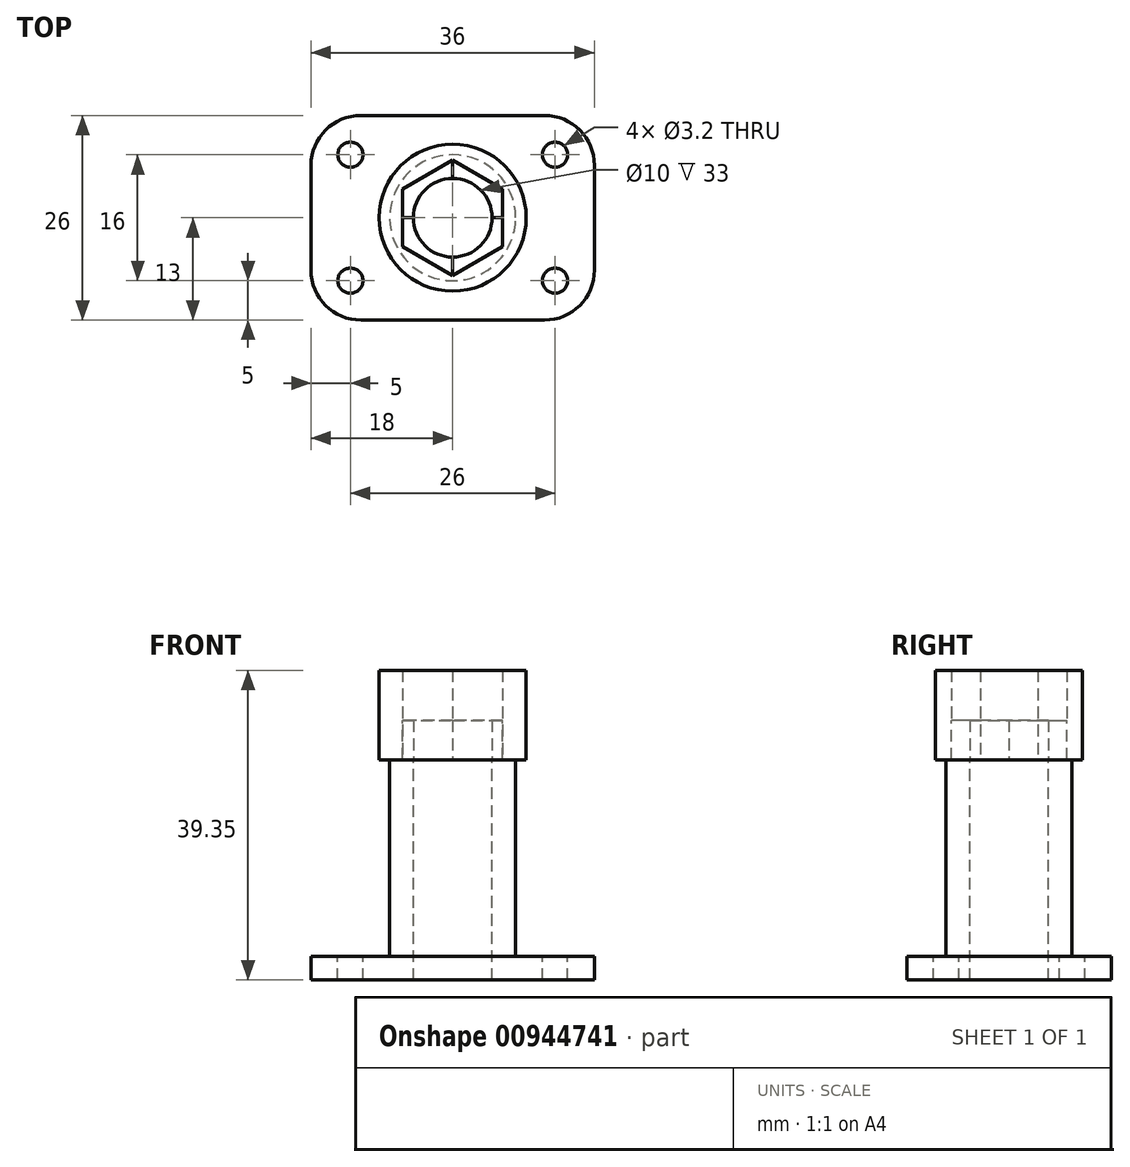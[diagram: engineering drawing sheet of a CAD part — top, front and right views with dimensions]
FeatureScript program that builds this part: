
annotation { "Feature Type Name" : "Feature", "Feature Type Description" : "" }
export const myFeature = defineFeature(function(context is Context, id is Id, definition is map)
    precondition{}
    {
        {
            var Q0;
            Q0=qCreatedBy(makeId("Top.planeOp"),FACE);
            var sketch = newSketch(context, id + "F0", { "sketchPlane" : qUnion([Q0])});
            skPoint(sketch, "E0.middle", {"position": v(0, 0) * mm});
            skCircle(sketch, "E1", {"center": v(0, 0) * mm, "radius": 5 * mm});
            skCircle(sketch, "E2.0", {"center": v(0, 0) * mm, "radius": 8 * mm});
            skLineSegment(sketch, "E3.bottom", {"start": v(-13, -8) * mm, "end": v(13, -8) * mm, "construction": true});
            skLineSegment(sketch, "E3.top", {"start": v(-13, 8) * mm, "end": v(13, 8) * mm, "construction": true});
            skLineSegment(sketch, "E3.left", {"start": v(-13, -8) * mm, "end": v(-13, 8) * mm, "construction": true});
            skLineSegment(sketch, "E3.right", {"start": v(13, -8) * mm, "end": v(13, 8) * mm, "construction": true});
            skLineSegment(sketch, "E4.0", {"start": v(-18, -6.65) * mm, "end": v(-18, 6.65) * mm});
            skLineSegment(sketch, "E4.1", {"start": v(-11.65, -13) * mm, "end": v(11.65, -13) * mm});
            skLineSegment(sketch, "E4.2", {"start": v(18, -6.65) * mm, "end": v(18, 6.65) * mm});
            skLineSegment(sketch, "E4.3", {"start": v(-11.65, 13) * mm, "end": v(11.65, 13) * mm});
            skPoint(sketch, "E5.visualSharp", {"position": v(-18, 13) * mm});
            skArc(sketch, "E5.filletArc", {"start": v(-11.65, 13) * mm, "mid": v(-16.14, 11.14) * mm, "end": v(-18, 6.65) * mm});
            skPoint(sketch, "E6.visualSharp", {"position": v(18, 13) * mm});
            skArc(sketch, "E6.filletArc", {"start": v(18, 6.65) * mm, "mid": v(16.14, 11.14) * mm, "end": v(11.65, 13) * mm});
            skPoint(sketch, "E7.visualSharp", {"position": v(18, -13) * mm});
            skArc(sketch, "E7.filletArc", {"start": v(11.65, -13) * mm, "mid": v(16.14, -11.14) * mm, "end": v(18, -6.65) * mm});
            skPoint(sketch, "E8.visualSharp", {"position": v(-18, -13) * mm});
            skArc(sketch, "E8.filletArc", {"start": v(-18, -6.65) * mm, "mid": v(-16.14, -11.14) * mm, "end": v(-11.65, -13) * mm});
            skLineSegment(sketch, "E9", {"start": v(0, 0) * mm, "end": v(-5, 0) * mm, "construction": true});
            skLineSegment(sketch, "E10", {"start": v(0, 0) * mm, "end": v(5, 0) * mm, "construction": true});
            skLineSegment(sketch, "E11", {"start": v(0, 0) * mm, "end": v(0, -5) * mm, "construction": true});
            skLineSegment(sketch, "E12", {"start": v(0, 0) * mm, "end": v(0, 5) * mm, "construction": true});
            skLineSegment(sketch, "E13", {"start": v(0, 5) * mm, "end": v(0, 8) * mm});
            skLineSegment(sketch, "E14", {"start": v(-5, 0) * mm, "end": v(-8, 0) * mm});
            skLineSegment(sketch, "E15", {"start": v(0, -5) * mm, "end": v(0, -8) * mm});
            skLineSegment(sketch, "E16", {"start": v(5, 0) * mm, "end": v(8, 0) * mm});
            skSolve(sketch);
        }
        {
            var Q0;
            Q0=makeQuery(id+"F0.imprint","IMPRINT",FACE,{"disambiguationData":[TD([[makeQuery(id+"F0.imprint","IMPRINT",EDGE,{"derivedFrom":sQuery(id+"F0.wireOp",EDGE,"E1")}),-1.0]])]});
            var Q1;
            Q1=makeQuery(id+"F0.imprint","IMPRINT",FACE,{"disambiguationData":[TD([[makeQuery(id+"F0.imprint","IMPRINT",EDGE,{"derivedFrom":sQuery(id+"F0.wireOp",EDGE,"E2.0")}),-1.0]])]});
            extrude(context, id + "F1", {"entities" : qUnion([Q0, Q1]), "oppositeDirection" : true, "depth" : 3 * mm, "offsetDistance" : 25 * mm});
        }
        {
            var Q0;
            {var subQ0=sQuery(id+"F0.wireOp",EDGE,"E14");Q0=makeQuery(id+"F0.imprint","IMPRINT",FACE,{"disambiguationData":[TD([[makeQuery(id+"F0.imprint","IMPRINT",EDGE,{"derivedFrom":subQ0}),1.0]])]});}
            var Q1;
            {var subQ0=sQuery(id+"F0.wireOp",EDGE,"E13");Q1=makeQuery(id+"F0.imprint","IMPRINT",FACE,{"disambiguationData":[TD([[makeQuery(id+"F0.imprint","IMPRINT",EDGE,{"derivedFrom":subQ0}),-1.0]])]});}
            extrude(context, id + "F2", {"entities" : qUnion([Q0, Q1]), "operationType" : NewBodyOperationType.ADD, "depth" : 25 * mm, "offsetDistance" : 25 * mm});
        }
        {
            var Q0;
            {var subQ0=sQuery(id+"F0.wireOp",EDGE,"E15");Q0=makeQuery(id+"F0.imprint","IMPRINT",FACE,{"disambiguationData":[TD([[makeQuery(id+"F0.imprint","IMPRINT",EDGE,{"derivedFrom":subQ0}),1.0]])]});}
            var Q1;
            {var subQ0=sQuery(id+"F0.wireOp",EDGE,"E13");Q1=makeQuery(id+"F0.imprint","IMPRINT",FACE,{"disambiguationData":[TD([[makeQuery(id+"F0.imprint","IMPRINT",EDGE,{"derivedFrom":subQ0}),1.0]])]});}
            var Q2;
            Q2=qCreatedBy(makeId("Top.planeOp"),FACE);
            var Q3;
            Q3=makeQuery(id+"F1.opExtrude","SWEPT_BODY",BODY,{"disambiguationData":[OSD([sQuery(id+"F0.wireOp",EDGE,"E1"),sQuery(id+"F0.wireOp",EDGE,"E4.0"),sQuery(id+"F0.wireOp",EDGE,"E4.1"),sQuery(id+"F0.wireOp",EDGE,"E4.2"),sQuery(id+"F0.wireOp",EDGE,"E4.3"),sQuery(id+"F0.wireOp",EDGE,"E5.filletArc"),sQuery(id+"F0.wireOp",EDGE,"E6.filletArc"),sQuery(id+"F0.wireOp",EDGE,"E7.filletArc"),sQuery(id+"F0.wireOp",EDGE,"E8.filletArc")])]});
            extrude(context, id + "F3", {"entities" : qUnion([Q0, Q1]), "depth" : 30 * mm, "offsetDistance" : 25 * mm});
        }
        {
            var Q0;
            Q0=sQuery(id+"F0.wireOp",VERTEX,"E3.right.start");
            var Q1;
            Q1=sQuery(id+"F0.wireOp",VERTEX,"E3.right.end");
            var Q2;
            Q2=sQuery(id+"F0.wireOp",VERTEX,"E3.top.start");
            var Q3;
            Q3=sQuery(id+"F0.wireOp",VERTEX,"E3.left.start");
            var Q4;
            Q4=makeQuery(id+"F1.opExtrude","SWEPT_BODY",BODY,{"disambiguationData":[OSD([sQuery(id+"F0.wireOp",EDGE,"E1"),sQuery(id+"F0.wireOp",EDGE,"E4.0"),sQuery(id+"F0.wireOp",EDGE,"E4.1"),sQuery(id+"F0.wireOp",EDGE,"E4.2"),sQuery(id+"F0.wireOp",EDGE,"E4.3"),sQuery(id+"F0.wireOp",EDGE,"E5.filletArc"),sQuery(id+"F0.wireOp",EDGE,"E6.filletArc"),sQuery(id+"F0.wireOp",EDGE,"E7.filletArc"),sQuery(id+"F0.wireOp",EDGE,"E8.filletArc")])]});
            hole(context, id + "F4", {"style" : HoleStyle.SIMPLE, "endStyle" : HoleEndStyle.THROUGH, "holeDiameter" : 3.2 * mm, "majorDiameter" : 5 * mm, "isTappedThrough" : true, "tappedDepth" : 12 * mm, "tapClearance" : 3, "locations" : qUnion([Q0, Q1, Q2, Q3]), "scope" : qUnion([Q4])});
        }
        {
            var Q0;
            Q0=makeQuery(id+"F3.opExtrude","CAP_FACE",FACE,{"disambiguationData":[OSD([sQuery(id+"F0.wireOp",EDGE,"E1"),sQuery(id+"F0.wireOp",EDGE,"E2.0"),sQuery(id+"F0.wireOp",EDGE,"E13"),sQuery(id+"F0.wireOp",EDGE,"E14")])],"isStart":false});
            var sketch = newSketch(context, id + "F5", { "sketchPlane" : qUnion([Q0])});
            skCircle(sketch, "E17.cCircle", {"center": v(0, 0) * mm, "radius": 6.35 * mm, "construction": true});
            skLineSegment(sketch, "E17.0", {"start": v(6.35, 3.67) * mm, "end": v(6.35, -3.67) * mm});
            skLineSegment(sketch, "E17.1", {"start": v(6.35, -3.67) * mm, "end": v(0, -7.33) * mm});
            skLineSegment(sketch, "E17.2", {"start": v(0, -7.33) * mm, "end": v(-6.35, -3.67) * mm});
            skLineSegment(sketch, "E17.3", {"start": v(-6.35, -3.67) * mm, "end": v(-6.35, 3.67) * mm});
            skLineSegment(sketch, "E17.4", {"start": v(-6.35, 3.67) * mm, "end": v(0, 7.33) * mm});
            skLineSegment(sketch, "E17.5", {"start": v(0, 7.33) * mm, "end": v(6.35, 3.67) * mm});
            skPoint(sketch, "E17.0.midPoint", {"position": v(6.35, 0) * mm});
            skCircle(sketch, "E18", {"center": v(0, 0) * mm, "radius": 9.33 * mm});
            skSolve(sketch);
        }
        {
            var Q0;
            Q0 = qSketchRegion(id + "F5", true);
            extrude(context, id + "F6", {"entities" : qUnion([Q0]), "operationType" : NewBodyOperationType.ADD, "depth" : 6.35 * mm, "offsetDistance" : 25 * mm});
        }
        {
            var Q0;
            Q0=makeQuery(id+"F6.opExtrude","CAP_FACE",FACE,{"disambiguationData":[OSD([sQuery(id+"F5.wireOp",EDGE,"E17.0"),sQuery(id+"F5.wireOp",EDGE,"E17.1"),sQuery(id+"F5.wireOp",EDGE,"E17.2"),sQuery(id+"F5.wireOp",EDGE,"E17.3"),sQuery(id+"F5.wireOp",EDGE,"E17.4"),sQuery(id+"F5.wireOp",EDGE,"E17.5"),sQuery(id+"F5.wireOp",EDGE,"E18")])],"isStart":true});
            extrude(context, id + "F7", {"entities" : qUnion([Q0]), "operationType" : NewBodyOperationType.ADD, "depth" : 5 * mm, "offsetDistance" : 25 * mm});
        }
    });
